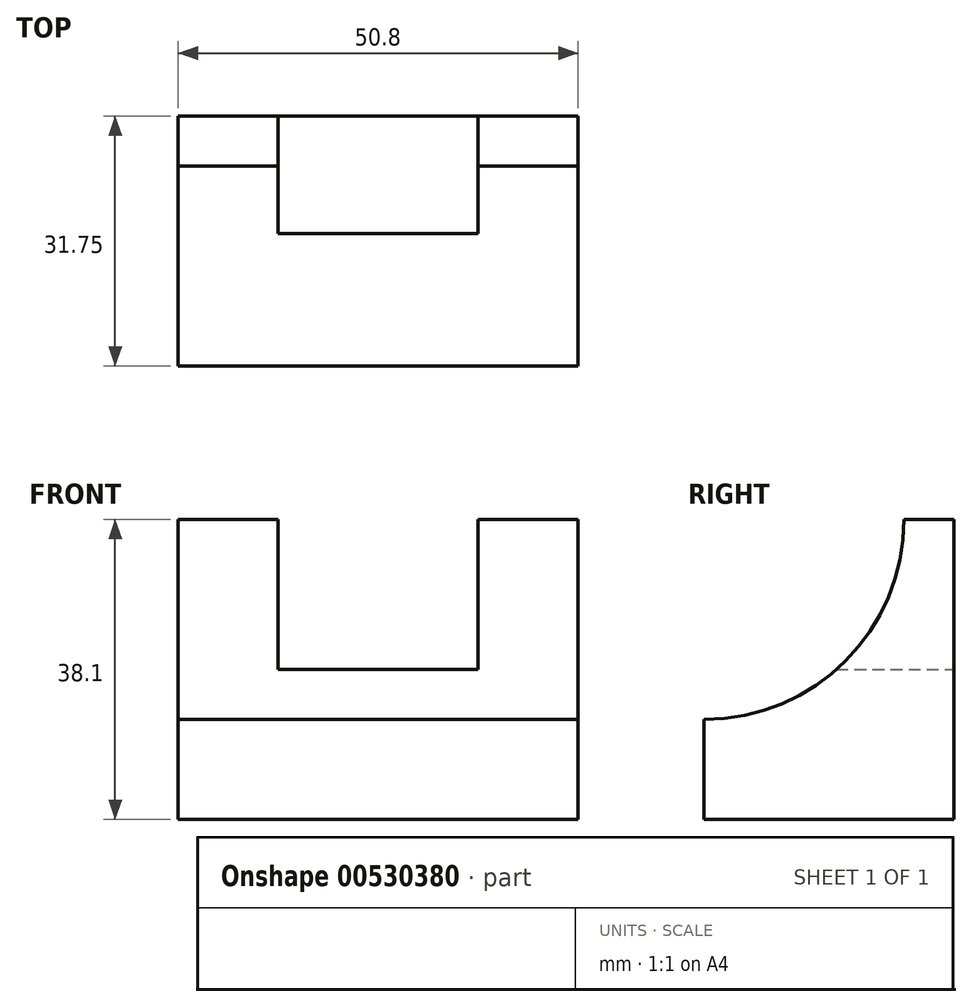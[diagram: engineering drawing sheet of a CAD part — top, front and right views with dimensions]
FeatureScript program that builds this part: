
annotation { "Feature Type Name" : "Feature", "Feature Type Description" : "" }
export const myFeature = defineFeature(function(context is Context, id is Id, definition is map)
    precondition{}
    {
        {
            var Q0;
            Q0=qCreatedBy(makeId("Right.planeOp"),FACE);
            var sketch = newSketch(context, id + "F0", { "sketchPlane" : qUnion([Q0])});
            skLineSegment(sketch, "E0", {"start": v(0, 38.1) * mm, "end": v(0, 0) * mm});
            skLineSegment(sketch, "E1", {"start": v(0, 0) * mm, "end": v(-31.75, 0) * mm});
            skLineSegment(sketch, "E2", {"start": v(-31.75, 0) * mm, "end": v(-31.75, 38.1) * mm});
            skLineSegment(sketch, "E3", {"start": v(-31.75, 38.1) * mm, "end": v(0, 38.1) * mm});
            skArc(sketch, "E4", {"start": v(-31.75, 12.7) * mm, "mid": v(-13.79, 20.14) * mm, "end": v(-6.35, 38.1) * mm});
            skSolve(sketch);
        }
        {
            var Q0;
            {var subQ4=sQuery(id+"F0.wireOp",EDGE,"E0");Q0=makeQuery(id+"F0.imprint","IMPRINT",FACE,{"disambiguationData":[TD([[makeQuery(id+"F0.imprint","IMPRINT",EDGE,{"derivedFrom":subQ4}),-1.0]])]});}
            extrude(context, id + "F1", {"entities" : qUnion([Q0]), "depth" : 50.8 * mm, "offsetDistance" : 25.4 * mm});
        }
        {
            var Q0;
            Q0=makeQuery(id+"F1.opExtrude","SWEPT_FACE",FACE,{"disambiguationData":[OSD([sQuery(id+"F0.wireOp",EDGE,"E0")])]});
            var sketch = newSketch(context, id + "F2", { "sketchPlane" : qUnion([Q0])});
            skLineSegment(sketch, "E5", {"start": v(-38.1, 38.1) * mm, "end": v(-38.1, 19.05) * mm});
            skLineSegment(sketch, "E6", {"start": v(-38.1, 19.05) * mm, "end": v(-12.7, 19.05) * mm});
            skLineSegment(sketch, "E7", {"start": v(-12.7, 19.05) * mm, "end": v(-12.7, 38.1) * mm});
            skLineSegment(sketch, "E8", {"start": v(-12.7, 38.1) * mm, "end": v(-38.1, 38.1) * mm});
            skSolve(sketch);
        }
        {
            var Q0;
            Q0=makeQuery(id+"F2.imprint","IMPRINT",FACE,{"disambiguationData":[TD([[makeQuery(id+"F2.imprint","IMPRINT",EDGE,{"derivedFrom":sQuery(id+"F2.wireOp",EDGE,"E5")}),1.0]])]});
            extrude(context, id + "F3", {"entities" : qUnion([Q0]), "operationType" : NewBodyOperationType.REMOVE, "endBound" : BoundingType.THROUGH_ALL, "oppositeDirection" : true, "depth" : 25.4 * mm, "offsetDistance" : 25.4 * mm});
        }
    });
